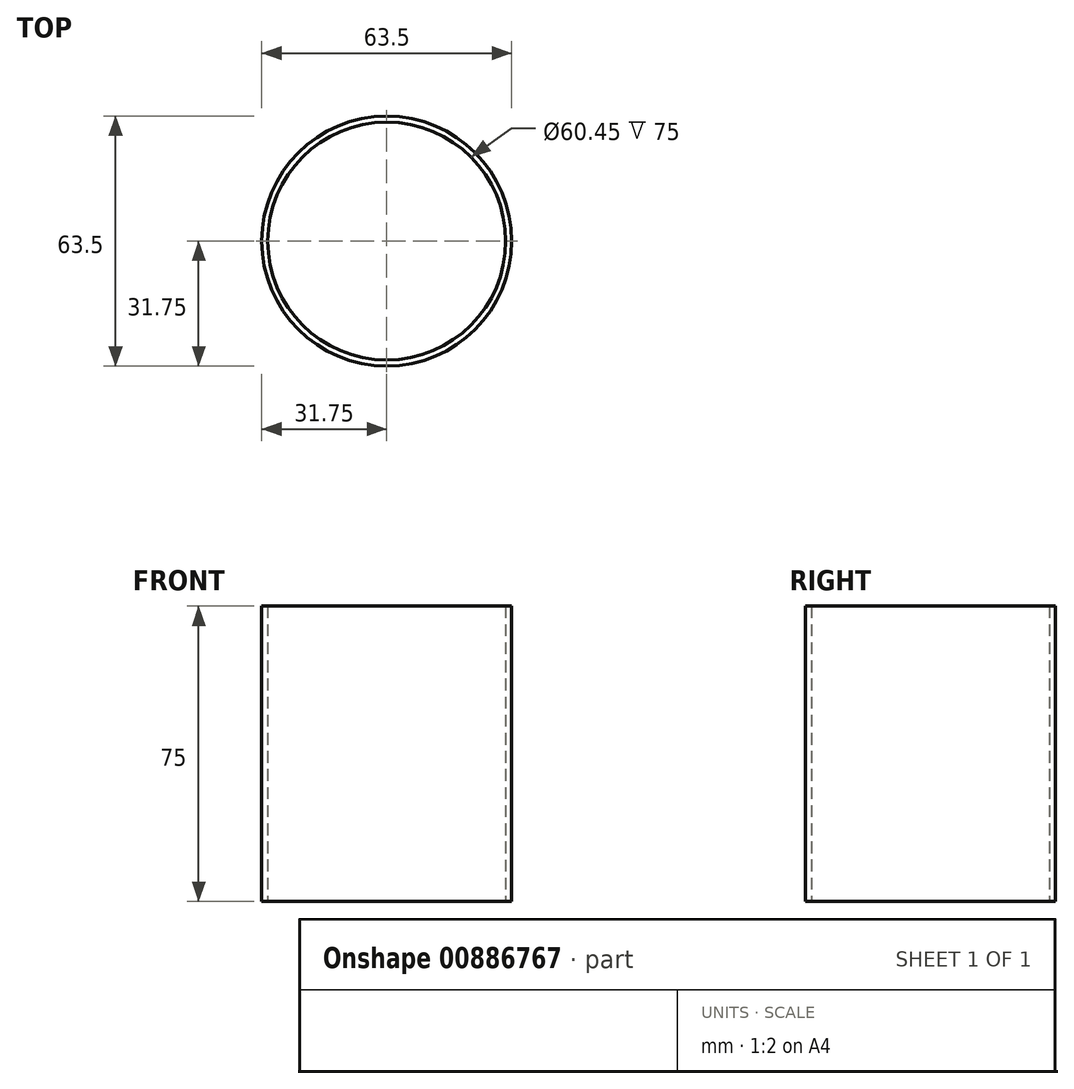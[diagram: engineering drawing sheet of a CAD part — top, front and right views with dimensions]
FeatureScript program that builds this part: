
annotation { "Feature Type Name" : "Feature", "Feature Type Description" : "" }
export const myFeature = defineFeature(function(context is Context, id is Id, definition is map)
    precondition{}
    {
        {
            var Q0;
            Q0=qCreatedBy(makeId("Top.planeOp"),FACE);
            var sketch = newSketch(context, id + "F0", { "sketchPlane" : qUnion([Q0])});
            skCircle(sketch, "E0", {"center": v(0, 0) * mm, "radius": 31.75 * mm});
            skCircle(sketch, "E1.0", {"center": v(0, 0) * mm, "radius": 30.23 * mm});
            skSolve(sketch);
        }
        {
            var Q0;
            Q0 = qSketchRegion(id + "F0", true);
            extrude(context, id + "F1", {"entities" : qUnion([Q0]), "depth" : 75 * mm, "offsetDistance" : 25 * mm});
        }
    });
